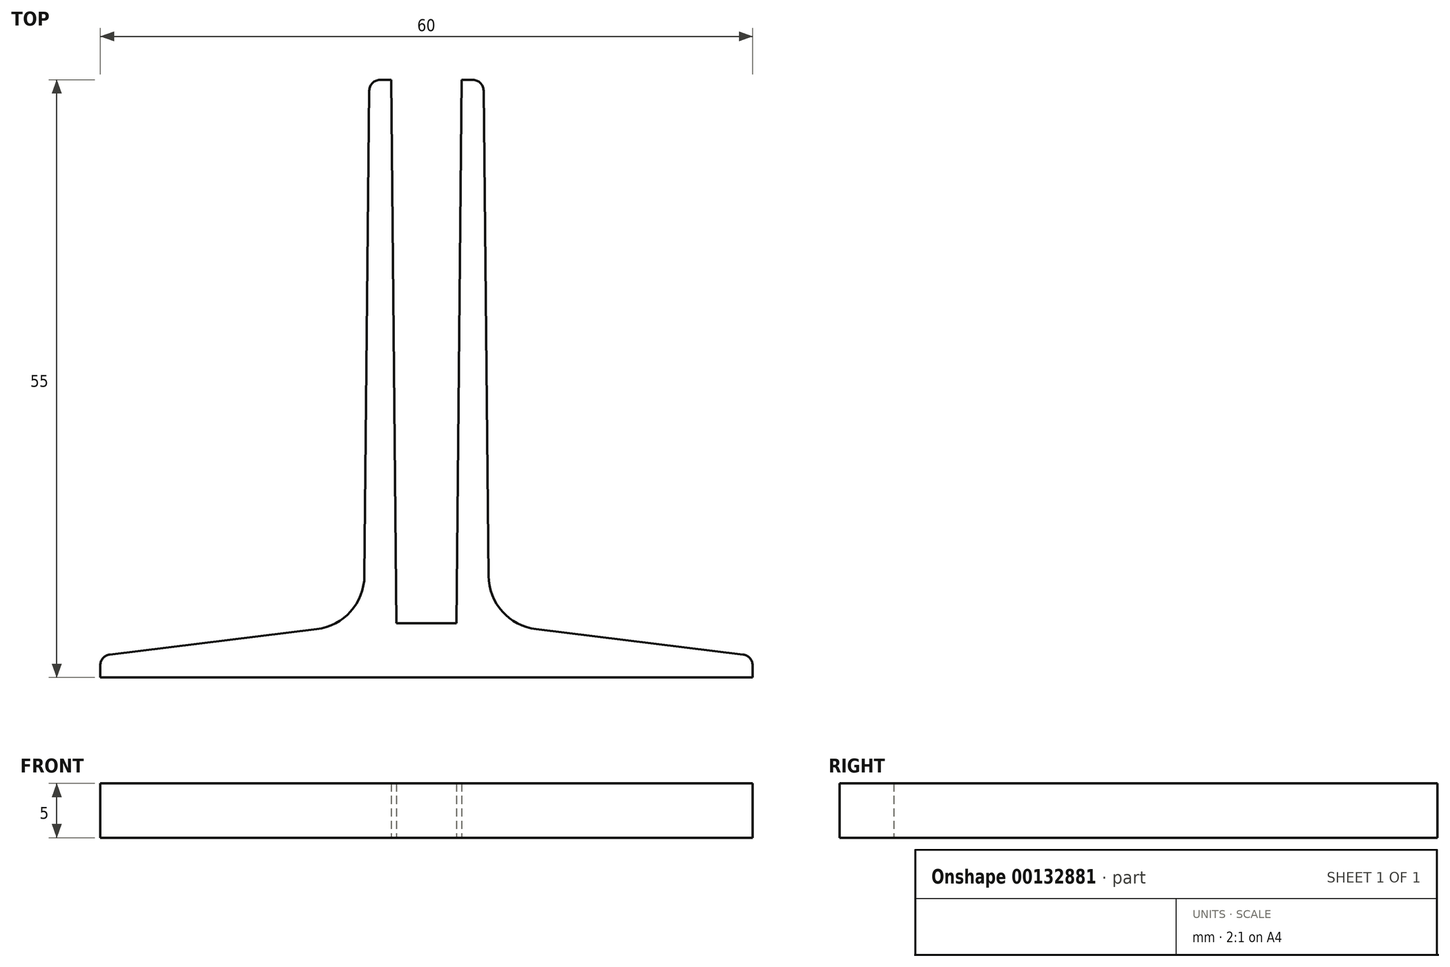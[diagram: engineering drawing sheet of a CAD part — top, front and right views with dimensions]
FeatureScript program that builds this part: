
annotation { "Feature Type Name" : "Feature", "Feature Type Description" : "" }
export const myFeature = defineFeature(function(context is Context, id is Id, definition is map)
    precondition{}
    {
        {
            var Q0;
            Q0=qCreatedBy(makeId("Top.planeOp"),FACE);
            var sketch = newSketch(context, id + "F0", { "sketchPlane" : qUnion([Q0])});
            skLineSegment(sketch, "E0", {"start": v(0, 0) * mm, "end": v(0, 50) * mm, "construction": true});
            skLineSegment(sketch, "E1", {"start": v(0, 0) * mm, "end": v(2.75, 0) * mm});
            skLineSegment(sketch, "E2", {"start": v(0, 50) * mm, "end": v(3.25, 50) * mm, "construction": true});
            skLineSegment(sketch, "E3", {"start": v(3.25, 50) * mm, "end": v(2.75, 0) * mm});
            skLineSegment(sketch, "E4", {"start": v(0, 0) * mm, "end": v(0, -5) * mm, "construction": true});
            skLineSegment(sketch, "E5", {"start": v(0, -5) * mm, "end": v(30, -5) * mm, "construction": true});
            skLineSegment(sketch, "E6", {"start": v(30, -5) * mm, "end": v(30, -3) * mm, "construction": true});
            skLineSegment(sketch, "E7", {"start": v(3.25, 50) * mm, "end": v(4.27, 49.99) * mm});
            skLineSegment(sketch, "E8", {"start": v(5.7, 4.35) * mm, "end": v(5.26, 49) * mm});
            skLineSegment(sketch, "E9", {"start": v(10.1, -0.56) * mm, "end": v(29.12, -2.9) * mm});
            skLineSegment(sketch, "E10", {"start": v(30, -5) * mm, "end": v(0, -5) * mm});
            skLineSegment(sketch, "E11", {"start": v(30, -3.88) * mm, "end": v(30, -5) * mm});
            skPoint(sketch, "E12.visualSharp", {"position": v(5.75, -0.03) * mm});
            skArc(sketch, "E12.filletArc", {"start": v(5.7, 4.35) * mm, "mid": v(6.98, 1.07) * mm, "end": v(10.1, -0.56) * mm});
            skPoint(sketch, "E13.visualSharp", {"position": v(5.25, 49.98) * mm});
            skArc(sketch, "E13.filletArc", {"start": v(5.26, 49) * mm, "mid": v(4.97, 49.7) * mm, "end": v(4.27, 49.99) * mm});
            skLineSegment(sketch, "E14.MirrorCS", {"start": v(-30, -3.88) * mm, "end": v(-30, -5) * mm});
            skLineSegment(sketch, "E15.MirrorCS", {"start": v(-3.25, 50) * mm, "end": v(-4.27, 49.99) * mm});
            skLineSegment(sketch, "E16.MirrorCS", {"start": v(0, -5) * mm, "end": v(-30, -5) * mm, "construction": true});
            skLineSegment(sketch, "E17.MirrorCS", {"start": v(-30, -5) * mm, "end": v(-30, -3) * mm, "construction": true});
            skArc(sketch, "E18.MirrorCS", {"start": v(-5.26, 49) * mm, "mid": v(-4.97, 49.7) * mm, "end": v(-4.27, 49.99) * mm});
            skLineSegment(sketch, "E19.MirrorCS", {"start": v(0, 0) * mm, "end": v(-2.75, 0) * mm});
            skArc(sketch, "E20.MirrorCS", {"start": v(-5.7, 4.35) * mm, "mid": v(-6.98, 1.07) * mm, "end": v(-10.1, -0.56) * mm});
            skLineSegment(sketch, "E21.MirrorCS", {"start": v(-30, -5) * mm, "end": v(0, -5) * mm});
            skPoint(sketch, "E22.MirrorP", {"position": v(-5.25, 49.98) * mm});
            skLineSegment(sketch, "E23.MirrorCS", {"start": v(-3.25, 50) * mm, "end": v(-2.75, 0) * mm});
            skPoint(sketch, "E24.MirrorP", {"position": v(-5.75, -0.03) * mm});
            skLineSegment(sketch, "E25.MirrorCS", {"start": v(-10.1, -0.56) * mm, "end": v(-29.12, -2.9) * mm});
            skLineSegment(sketch, "E26.MirrorCS", {"start": v(-5.7, 4.35) * mm, "end": v(-5.26, 49) * mm});
            skPoint(sketch, "E27.visualSharp", {"position": v(30, -3) * mm});
            skArc(sketch, "E27.filletArc", {"start": v(30, -3.88) * mm, "mid": v(29.75, -3.22) * mm, "end": v(29.12, -2.9) * mm});
            skPoint(sketch, "E28.visualSharp", {"position": v(-30, -3) * mm});
            skArc(sketch, "E28.filletArc", {"start": v(-29.12, -2.9) * mm, "mid": v(-29.75, -3.22) * mm, "end": v(-30, -3.88) * mm});
            skSolve(sketch);
        }
        {
            var Q0;
            Q0=makeQuery(id+"F0.imprint","IMPRINT",FACE,{"disambiguationData":[TD([[makeQuery(id+"F0.imprint","IMPRINT",EDGE,{"derivedFrom":sQuery(id+"F0.wireOp",EDGE,"E1")}),-1.0]])]});
            extrude(context, id + "F1", {"entities" : qUnion([Q0]), "depth" : 5 * mm});
        }
    });
